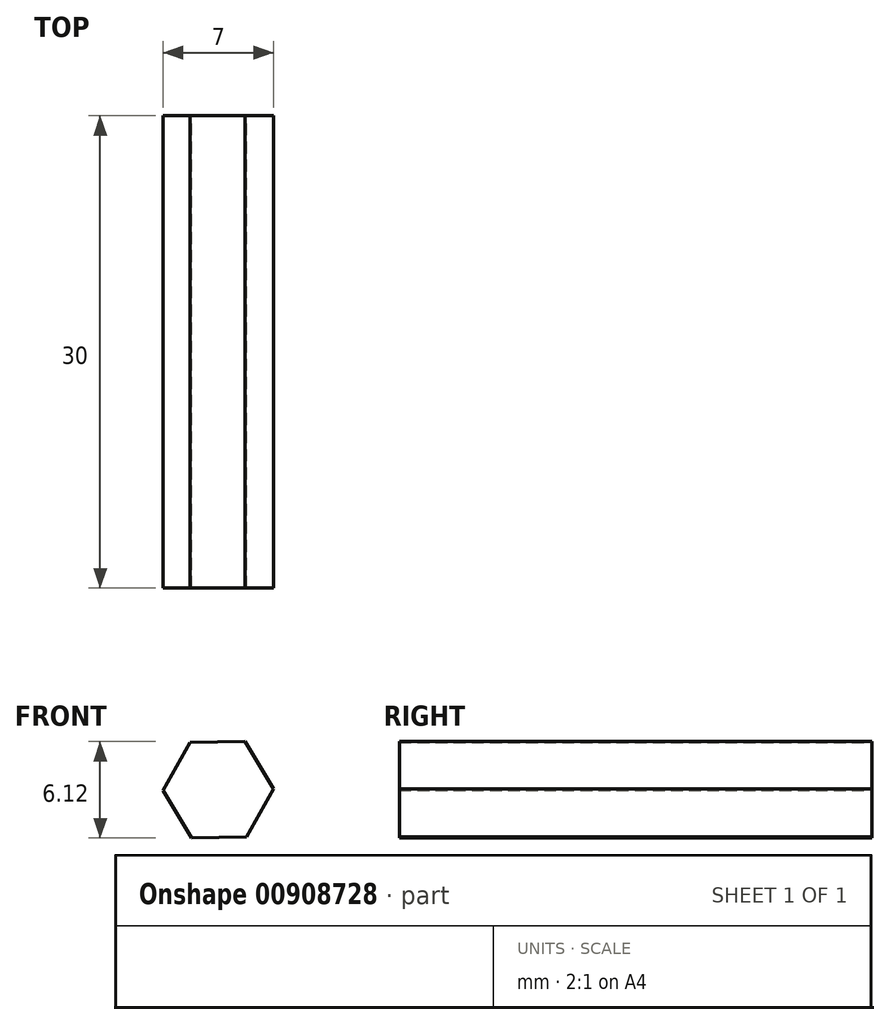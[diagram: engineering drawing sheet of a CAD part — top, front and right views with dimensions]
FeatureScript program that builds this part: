
annotation { "Feature Type Name" : "Feature", "Feature Type Description" : "" }
export const myFeature = defineFeature(function(context is Context, id is Id, definition is map)
    precondition{}
    {
        {
            var Q0;
            Q0=qCreatedBy(makeId("Front.planeOp"),FACE);
            var sketch = newSketch(context, id + "F0", { "sketchPlane" : qUnion([Q0])});
            skLineSegment(sketch, "E0.0", {"start": v(-3.5, -0.05) * mm, "end": v(-1.8, 3) * mm});
            skLineSegment(sketch, "E0.1", {"start": v(-1.8, 3) * mm, "end": v(1.7, 3.06) * mm});
            skLineSegment(sketch, "E0.2", {"start": v(1.7, 3.06) * mm, "end": v(3.5, 0.05) * mm});
            skLineSegment(sketch, "E0.3", {"start": v(3.5, 0.05) * mm, "end": v(1.8, -3) * mm});
            skLineSegment(sketch, "E0.4", {"start": v(1.8, -3) * mm, "end": v(-1.7, -3.06) * mm});
            skLineSegment(sketch, "E0.5", {"start": v(-1.7, -3.06) * mm, "end": v(-3.5, -0.05) * mm});
            skLineSegment(sketch, "E1", {"start": v(-3.5, -0.05) * mm, "end": v(3.5, 0.05) * mm, "construction": true});
            skSolve(sketch);
        }
        {
            var Q0;
            Q0=makeQuery(id+"F0.imprint","IMPRINT",FACE,{"disambiguationData":[TD([[makeQuery(id+"F0.imprint","IMPRINT",EDGE,{"derivedFrom":sQuery(id+"F0.wireOp",EDGE,"E0.0")}),-1.0]])]});
            extrude(context, id + "F1", {"entities" : qUnion([Q0]), "depth" : 30 * mm, "offsetDistance" : 25 * mm, "symmetric" : true});
        }
    });
